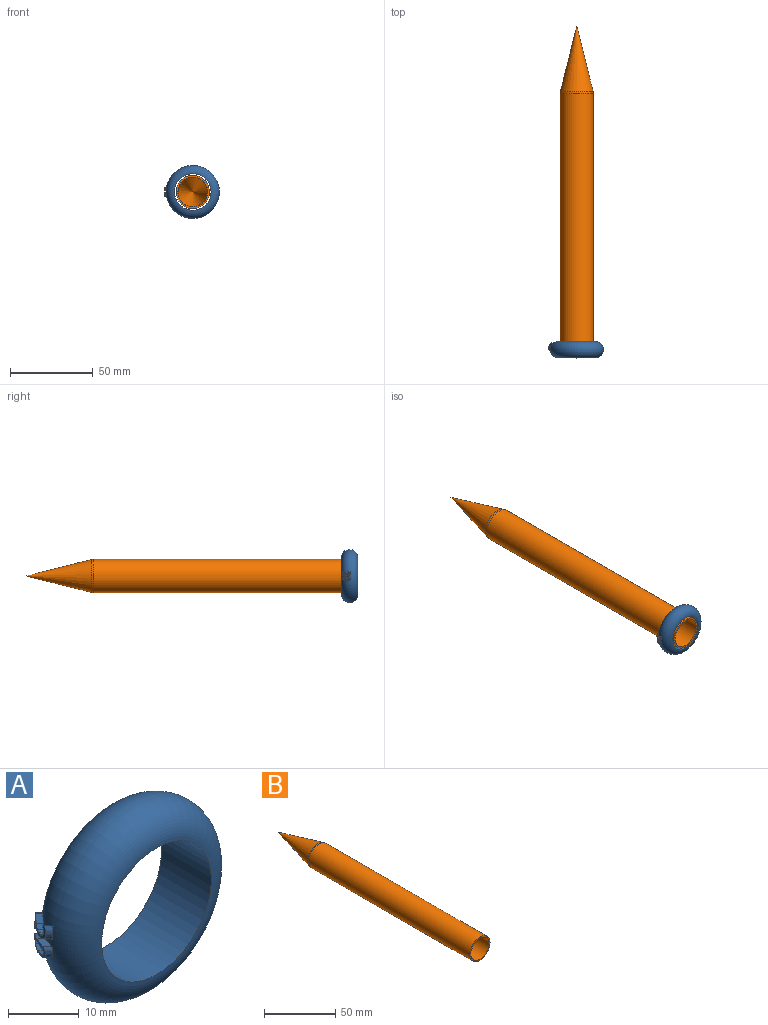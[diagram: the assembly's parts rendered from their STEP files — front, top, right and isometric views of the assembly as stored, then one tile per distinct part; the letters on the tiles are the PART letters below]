
ASSEMBLY  parts=2 mates=1
PART A: 42 faces, bbox 34.8x10x34.7 mm
  f0: extruded ~2.55x2.5mm, area 1.8mm2, adj f1,f15,f16,f17,f41
  f1: extruded ~2.09x2.07mm, area 1.6mm2, adj f0,f2,f17,f41
  f2: extruded ~1.19x1.11mm, area 1.1mm2, adj f1,f3,f17,f41
  f3: extruded ~1.09x1.08mm, area 1.1mm2, adj f2,f4,f17,f41
  f4: extruded ~2.08x2.04mm, area 1.6mm2, adj f3,f5,f17,f41
  f5: extruded ~2.54x2.52mm, area 1.8mm2, adj f4,f14,f17,f41
  f6: extruded ~1.42x1.36mm, area 1mm2, adj f7,f13,f15,f17,f41
  f7: extruded ~2.18x2.17mm, area 1.4mm2, adj f6,f8,f17,f41
  f8: extruded ~1.85x1.82mm, area 1.3mm2, adj f7,f9,f17,f41
  f9: extruded ~1.03x0.96mm, area 0.8mm2, adj f8,f10,f17,f41
  f10: extruded ~1.08x1.02mm, area 0.8mm2, adj f9,f11,f17,f41
  f11: extruded ~1.87x1.86mm, area 1.3mm2, adj f10,f12,f17,f41
  f12: extruded ~2.18x2.15mm, area 1.5mm2, adj f11,f13,f17,f41
  f13: extruded ~1.35x1.29mm, area 1mm2, adj f6,f12,f15,f17,f41
  f14: extruded ~1.4x1.31mm, area 1.2mm2, adj f5,f15,f16,f17,f41
  f15: plane 1.92x0.52mm, normal (0.7,-0.71,0.07), area 0.6mm2, adj f0,f6,f13,f14,f16,f41
  f16: extruded ~1.28x1.19mm, area 1.3mm2, adj f0,f14,f15,f17
  f17: torus R=11mm, axis (0,-1,0), area 4.1mm2, adj f0,f1,f2,f3,f4,f5,f6,f7
  f18: plane 0.73x0.72mm, normal (-0.1,0,-1), area 0mm2, adj f19,f35,f39,f41
  f19: plane 1.42x1.32mm, normal (0.43,0.51,-0.75), area 1.2mm2, adj f18,f20,f39,f41
  f20: extruded ~1.71x1.64mm, area 1.3mm2, adj f19,f21,f39,f41
  f21: extruded ~1.64x1.63mm, area 0.9mm2, adj f20,f22,f39,f41
  f22: extruded ~1.71x1.67mm, area 1.1mm2, adj f21,f36,f37,f39,f41
  f23: plane 1.27x0.93mm, normal (0.51,0.43,0.74), area 0.5mm2, adj f24,f36,f38,f39,f41
  f24: extruded ~1.3x1.26mm, area 0.7mm2, adj f23,f25,f39,f41
  f25: extruded ~1.03x0.99mm, area 0.6mm2, adj f24,f26,f36,f39,f41
  f26: extruded ~1.12x1.07mm, area 0.7mm2, adj f25,f27,f36,f39,f41
  f27: extruded ~1.48x1.45mm, area 0.7mm2, adj f26,f28,f39,f41
  f28: extruded ~1.29x1.29mm, area 0.5mm2, adj f27,f29,f39,f41
  f29: extruded ~1.22x1.2mm, area 0.5mm2, adj f28,f30,f39,f41
  f30: extruded ~1.45x1.4mm, area 1mm2, adj f29,f31,f39,f41
  f31: plane 1.56x1.45mm, normal (-0.43,-0.5,0.76), area 1.5mm2, adj f30,f32,f39,f41
  f32: plane 1x0.96mm, normal (0.1,0,1), area 0.4mm2, adj f31,f33,f39,f41
  f33: plane 2.61x0.97mm, normal (0.7,0.71,-0.07), area 2.6mm2, adj f32,f34,f39,f41
  f34: plane 1.02x0.98mm, normal (-0.1,0,-1), area 0.4mm2, adj f33,f35,f39,f41
  f35: plane 2.06x0.89mm, normal (-0.7,-0.71,0.07), area 2mm2, adj f18,f34,f39,f41
  f36: plane 2.19x0.52mm, normal (0.7,-0.71,-0.07), area 0.7mm2, adj f22,f23,f25,f26,f37,f38,f41
  f37: extruded ~1.03x0.96mm, area 1mm2, adj f22,f36,f38,f39
  f38: extruded ~1.32x1.22mm, area 1.4mm2, adj f23,f36,f37,f39
  f39: torus R=11mm, axis (0,-1,0), area 3.7mm2, adj f18,f19,f20,f21,f22,f23,f24,f25
  f40: cylinder r=11mm len=22mm, axis (0,1,0), area 691.2mm2, adj f41
  f41: torus R=11mm, axis (0,-1,0), area 1393.2mm2, adj f0,f1,f2,f3,f4,f5,f6,f7
PART B: 8 faces, bbox 21.6x200x21.6 mm
  f0: cylinder r=9mm len=160mm, axis (0,1,0), area 9047.8mm2, adj f2,f4
  f1: cylinder r=10mm len=159.38mm, axis (0,1,0), area 10014.4mm2, adj f2,f5
  f2: plane 20x20mm, normal (0,-1,0), area 59.7mm2, adj f0,f1
  f3: cone r=10mm half-angle=14deg, axis (0,-1,0), area 1256.9mm2, adj f5
  f4: plane 18x18mm, normal (0,-1,0), area 2.7mm2, adj f0,f6
  f5: torus R=5mm, axis (0,-1,0), area 76.6mm2, adj f1,f3
  f6: torus R=5mm, axis (0,-1,0), area 20.3mm2, adj f4,f7
  f7: cone r=9.03mm half-angle=14deg, axis (0,-1,0), area 1021.5mm2, adj f6
PLACE A t=(-38.83,-57.77,-60.09)mm
PLACE B t=(-38.83,92.23,-60.09)mm
MATE fastened B.f0 <-> A.f40  axis (0,-1,0) through (-38.83,-67.77,-60.09)mm
